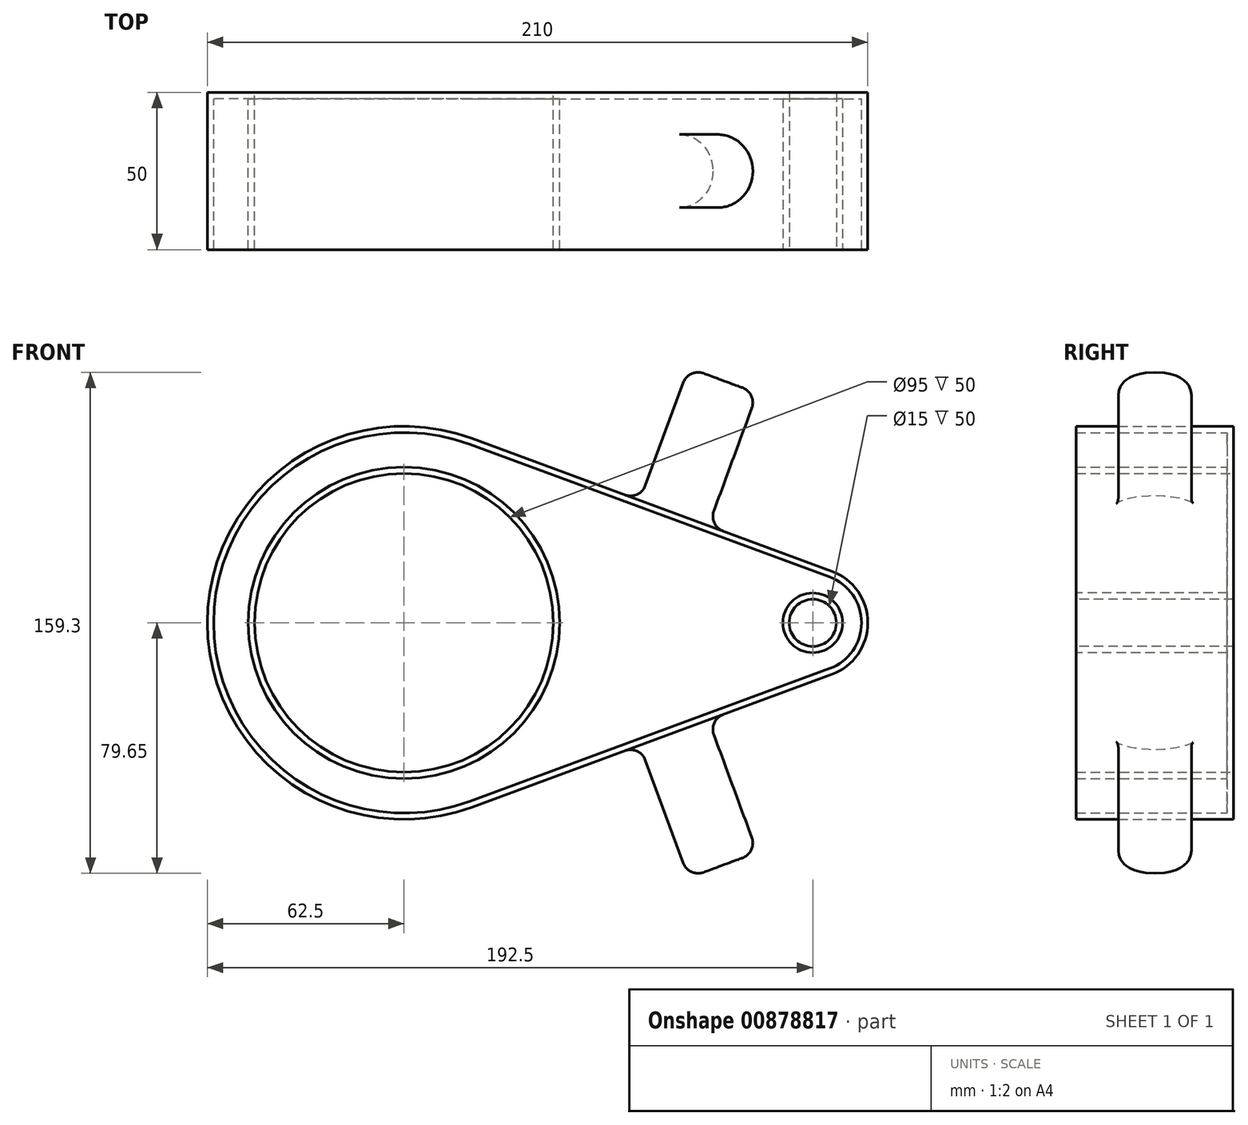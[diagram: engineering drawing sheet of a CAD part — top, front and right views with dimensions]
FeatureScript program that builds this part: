
annotation { "Feature Type Name" : "Feature", "Feature Type Description" : "" }
export const myFeature = defineFeature(function(context is Context, id is Id, definition is map)
    precondition{}
    {
        {
            var Q0;
            Q0=qCreatedBy(makeId("Front.planeOp"),FACE);
            var sketch = newSketch(context, id + "F0", { "sketchPlane" : qUnion([Q0])});
            skCircle(sketch, "E0", {"center": v(0, 0) * mm, "radius": 62.5 * mm});
            skCircle(sketch, "E1", {"center": v(130, 0) * mm, "radius": 17.5 * mm});
            skLineSegment(sketch, "E2", {"start": v(21.63, 58.64) * mm, "end": v(136.06, 16.42) * mm});
            skLineSegment(sketch, "E3", {"start": v(21.63, -58.64) * mm, "end": v(136.06, -16.42) * mm});
            skCircle(sketch, "E4", {"center": v(0, 0) * mm, "radius": 47.5 * mm});
            skSolve(sketch);
        }
        {
            var Q0;
            Q0 = qSketchRegion(id + "F0", true);
            extrude(context, id + "F1", {"entities" : qUnion([Q0]), "depth" : 50 * mm, "offsetDistance" : 25 * mm});
        }
        {
            var Q0;
            Q0=makeQuery(id+"F1.opExtrude","SWEPT_FACE",FACE,{"disambiguationData":[OSD([sQuery(id+"F0.wireOp",EDGE,"E2")])]});
            var sketch = newSketch(context, id + "F2", { "sketchPlane" : qUnion([Q0])});
            skCircle(sketch, "E5", {"center": v(68.52, -25) * mm, "radius": 11.63 * mm});
            skPoint(sketch, "E5.centerSnap0", {"position": v(121.96, -25) * mm});
            skSolve(sketch);
        }
        {
            var Q0;
            Q0=makeQuery(id+"F2.imprint","IMPRINT",FACE,{"disambiguationData":[TD([[makeQuery(id+"F2.imprint","IMPRINT",EDGE,{"derivedFrom":sQuery(id+"F2.wireOp",EDGE,"E5")}),1.0]])]});
            extrude(context, id + "F3", {"entities" : qUnion([Q0]), "depth" : 44.9 * mm, "offsetDistance" : 25 * mm});
        }
        {
            var Q0;
            Q0=makeQuery(id+"F3.opExtrude","CAP_EDGE",EDGE,{"disambiguationData":[OSD([sQuery(id+"F2.wireOp",EDGE,"E5")])],"isStart":false});
            var Q1;
            Q1=makeQuery(id+"F3.opExtrude","CAP_EDGE",EDGE,{"disambiguationData":[OSD([sQuery(id+"F2.wireOp",EDGE,"E5")])],"isStart":true});
            fillet(context, id + "F4", {"entities" : qUnion([Q0, Q1]), "radius" : 5 * mm, "tangentPropagation" : true, "allowEdgeOverflow" : false});
        }
        {
            var Q0;
            Q0=makeQuery(id+"F1.opExtrude","CAP_FACE",FACE,{"disambiguationData":[OSD([sQuery(id+"F0.wireOp",EDGE,"E0"),sQuery(id+"F0.wireOp",EDGE,"E1"),sQuery(id+"F0.wireOp",EDGE,"E2"),sQuery(id+"F0.wireOp",EDGE,"E3"),sQuery(id+"F0.wireOp",EDGE,"E4")])],"isStart":false});
            var sketch = newSketch(context, id + "F5", { "sketchPlane" : qUnion([Q0])});
            skCircle(sketch, "E6", {"center": v(130, 0) * mm, "radius": 7.5 * mm});
            skSolve(sketch);
        }
        {
            var Q0;
            Q0 = qSketchRegion(id + "F5", true);
            extrude(context, id + "F6", {"entities" : qUnion([Q0]), "operationType" : NewBodyOperationType.REMOVE, "endBound" : BoundingType.THROUGH_ALL, "oppositeDirection" : true, "depth" : 25 * mm, "offsetDistance" : 25 * mm});
        }
        {
            var Q0;
            Q0=makeQuery(id+"F1.opExtrude","CAP_FACE",FACE,{"disambiguationData":[OSD([sQuery(id+"F0.wireOp",EDGE,"E0"),sQuery(id+"F0.wireOp",EDGE,"E1"),sQuery(id+"F0.wireOp",EDGE,"E2"),sQuery(id+"F0.wireOp",EDGE,"E3"),sQuery(id+"F0.wireOp",EDGE,"E4")])],"isStart":false});
            shell(context, id + "F7", {"entities" : qUnion([Q0]), "thickness" : 2 * mm});
        }
        {
            var Q0;
            Q0=makeQuery(id+"F3.opExtrude","SWEPT_BODY",BODY,{"disambiguationData":[OSD([sQuery(id+"F2.wireOp",EDGE,"E5")])]});
            var Q1;
            Q1=qCreatedBy(makeId("Top.planeOp"),FACE);
            mirror(context, id + "F8", {"operationType" : NewBodyOperationType.ADD, "entities" : qUnion([Q0]), "mirrorPlane" : qUnion([Q1])});
        }
        {
            var Q0;
            {var subQ0=sQuery(id+"F2.wireOp",EDGE,"E5");Q0=makeQuery(id+"F4.opFillet","BLEND_FACE",FACE,{"disambiguationData":[OSD([subQ0]),TDD([makeQuery(id+"F3.opExtrude","CAP_EDGE",EDGE,{"disambiguationData":[OSD([subQ0])],"isStart":true})])]});}
            var Q1;
            {var subQ0=sQuery(id+"F2.wireOp",EDGE,"E5");Q1=makeQuery(id+"F8.opPattern","COPY",FACE,{"derivedFrom":makeQuery(id+"F4.opFillet","BLEND_FACE",FACE,{"disambiguationData":[OSD([subQ0]),TDD([makeQuery(id+"F3.opExtrude","CAP_EDGE",EDGE,{"disambiguationData":[OSD([subQ0])],"isStart":true})])]}),"instanceName":"1"});}
            fillet(context, id + "F9", {"entities" : qUnion([Q0, Q1]), "radius" : 5 * mm, "tangentPropagation" : true, "allowEdgeOverflow" : false});
        }
    });
